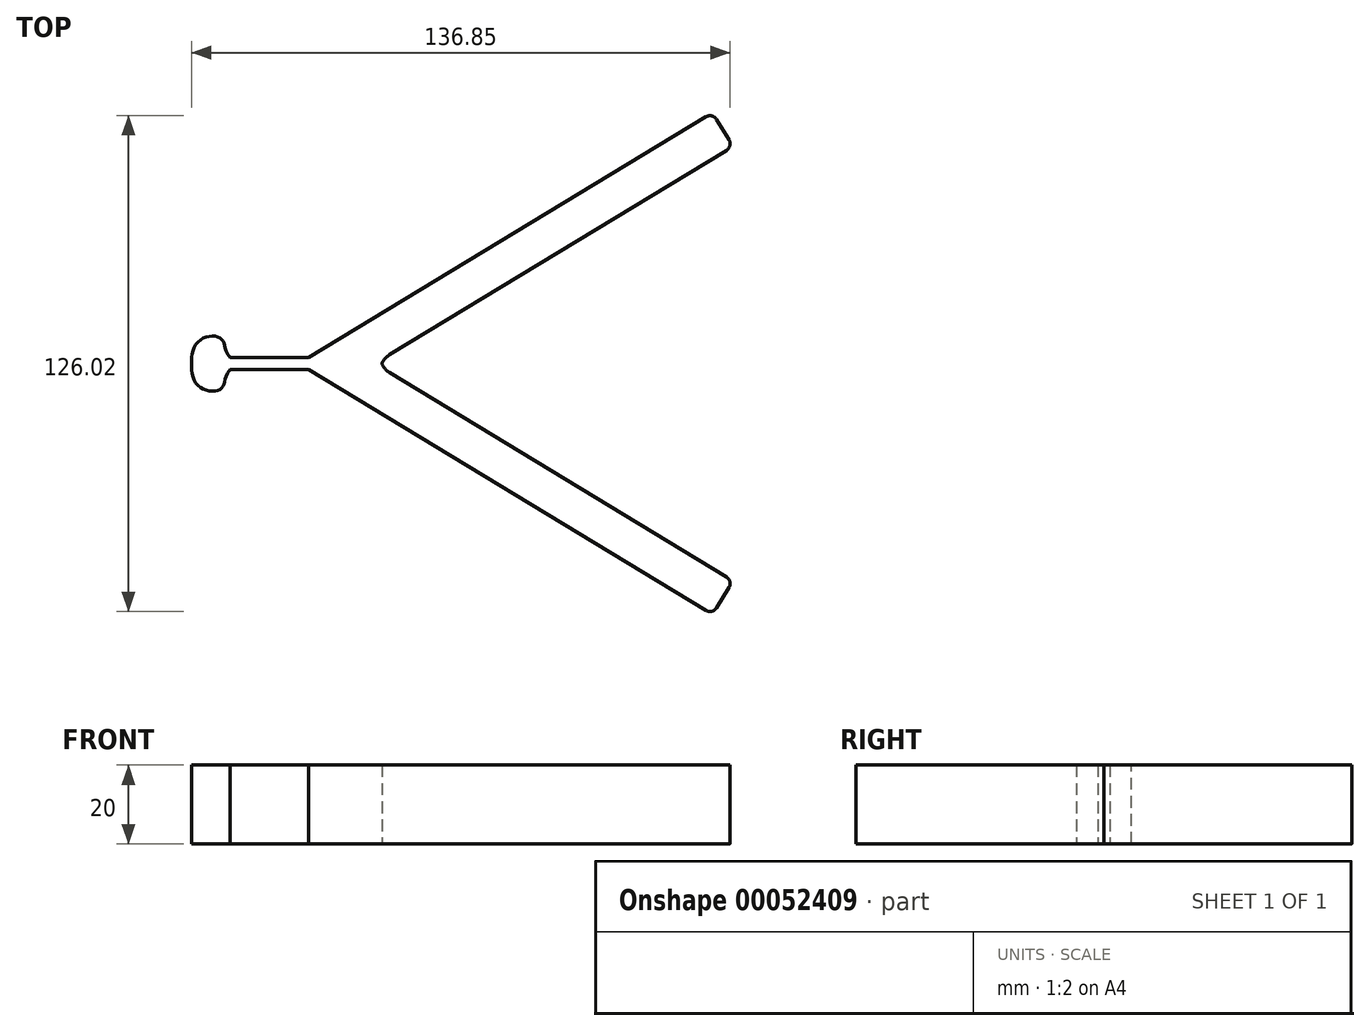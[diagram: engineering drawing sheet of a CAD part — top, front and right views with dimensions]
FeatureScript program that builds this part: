
annotation { "Feature Type Name" : "Feature", "Feature Type Description" : "" }
export const myFeature = defineFeature(function(context is Context, id is Id, definition is map)
    precondition{}
    {
        {
            var Q0;
            Q0=qCreatedBy(makeId("Top.planeOp"),FACE);
            var sketch = newSketch(context, id + "F0", { "sketchPlane" : qUnion([Q0])});
            skLineSegment(sketch, "E0", {"start": v(106.74, 56.92) * mm, "end": v(103.62, 62.05) * mm});
            skLineSegment(sketch, "E1", {"start": v(100.88, 62.72) * mm, "end": v(0, 1.5) * mm});
            skLineSegment(sketch, "E2", {"start": v(0, 1.5) * mm, "end": v(-20, 1.5) * mm});
            skFitSpline(sketch, "E3", {"points": [v(-29.82, 0) * mm, v(-28.48, 5.16) * mm, v(-24.17, 7) * mm, v(-21.75, 5.7) * mm, v(-20, 1.5) * mm], "startDerivative": vector(0, 17.83) * mm, "endDerivative": vector(17.52, -21.46) * mm});
            skLineSegment(sketch, "E4", {"start": v(18.16, -1.99) * mm, "end": v(18.16, 0) * mm});
            skLineSegment(sketch, "E5", {"start": v(20.57, 2.29) * mm, "end": v(106.07, 54.17) * mm});
            skLineSegment(sketch, "E6.MirrorCS", {"start": v(18.16, 1.99) * mm, "end": v(18.16, 0) * mm});
            skLineSegment(sketch, "E7.MirrorCS", {"start": v(20.57, -2.29) * mm, "end": v(106.07, -54.17) * mm});
            skLineSegment(sketch, "E8.MirrorCS", {"start": v(106.74, -56.92) * mm, "end": v(103.62, -62.05) * mm});
            skLineSegment(sketch, "E9.MirrorCS", {"start": v(100.88, -62.72) * mm, "end": v(0, -1.5) * mm});
            skLineSegment(sketch, "E10.MirrorCS", {"start": v(0, -1.5) * mm, "end": v(-20, -1.5) * mm});
            skFitSpline(sketch, "E11.MirrorCS", {"points": [v(-29.82, 0) * mm, v(-28.48, -5.16) * mm, v(-24.17, -7) * mm, v(-21.75, -5.7) * mm, v(-20, -1.5) * mm], "startDerivative": vector(0, -17.83) * mm, "endDerivative": vector(17.52, 21.46) * mm});
            skPoint(sketch, "E12.visualSharp", {"position": v(18.16, 0.82) * mm});
            skArc(sketch, "E12.filletArc", {"start": v(20.57, 2.29) * mm, "mid": v(18.8, 0.46) * mm, "end": v(18.16, -1.99) * mm});
            skPoint(sketch, "E13.visualSharp", {"position": v(18.16, -0.82) * mm});
            skArc(sketch, "E13.filletArc", {"start": v(18.16, 1.99) * mm, "mid": v(18.8, -0.46) * mm, "end": v(20.57, -2.29) * mm});
            skPoint(sketch, "E14.visualSharp", {"position": v(102.59, 63.76) * mm});
            skArc(sketch, "E14.filletArc", {"start": v(103.62, 62.05) * mm, "mid": v(102.4, 62.95) * mm, "end": v(100.88, 62.72) * mm});
            skPoint(sketch, "E15.visualSharp", {"position": v(107.78, 55.2) * mm});
            skArc(sketch, "E15.filletArc", {"start": v(106.07, 54.17) * mm, "mid": v(106.97, 55.4) * mm, "end": v(106.74, 56.92) * mm});
            skPoint(sketch, "E16.visualSharp", {"position": v(102.59, -63.76) * mm});
            skArc(sketch, "E16.filletArc", {"start": v(100.88, -62.72) * mm, "mid": v(102.4, -62.95) * mm, "end": v(103.62, -62.05) * mm});
            skPoint(sketch, "E17.visualSharp", {"position": v(107.78, -55.2) * mm});
            skArc(sketch, "E17.filletArc", {"start": v(106.74, -56.92) * mm, "mid": v(106.97, -55.4) * mm, "end": v(106.07, -54.17) * mm});
            skSolve(sketch);
        }
        {
            var Q0;
            Q0 = qSketchRegion(id + "F0", true);
            extrude(context, id + "F1", {"entities" : qUnion([Q0]), "depth" : 20 * mm});
        }
    });
